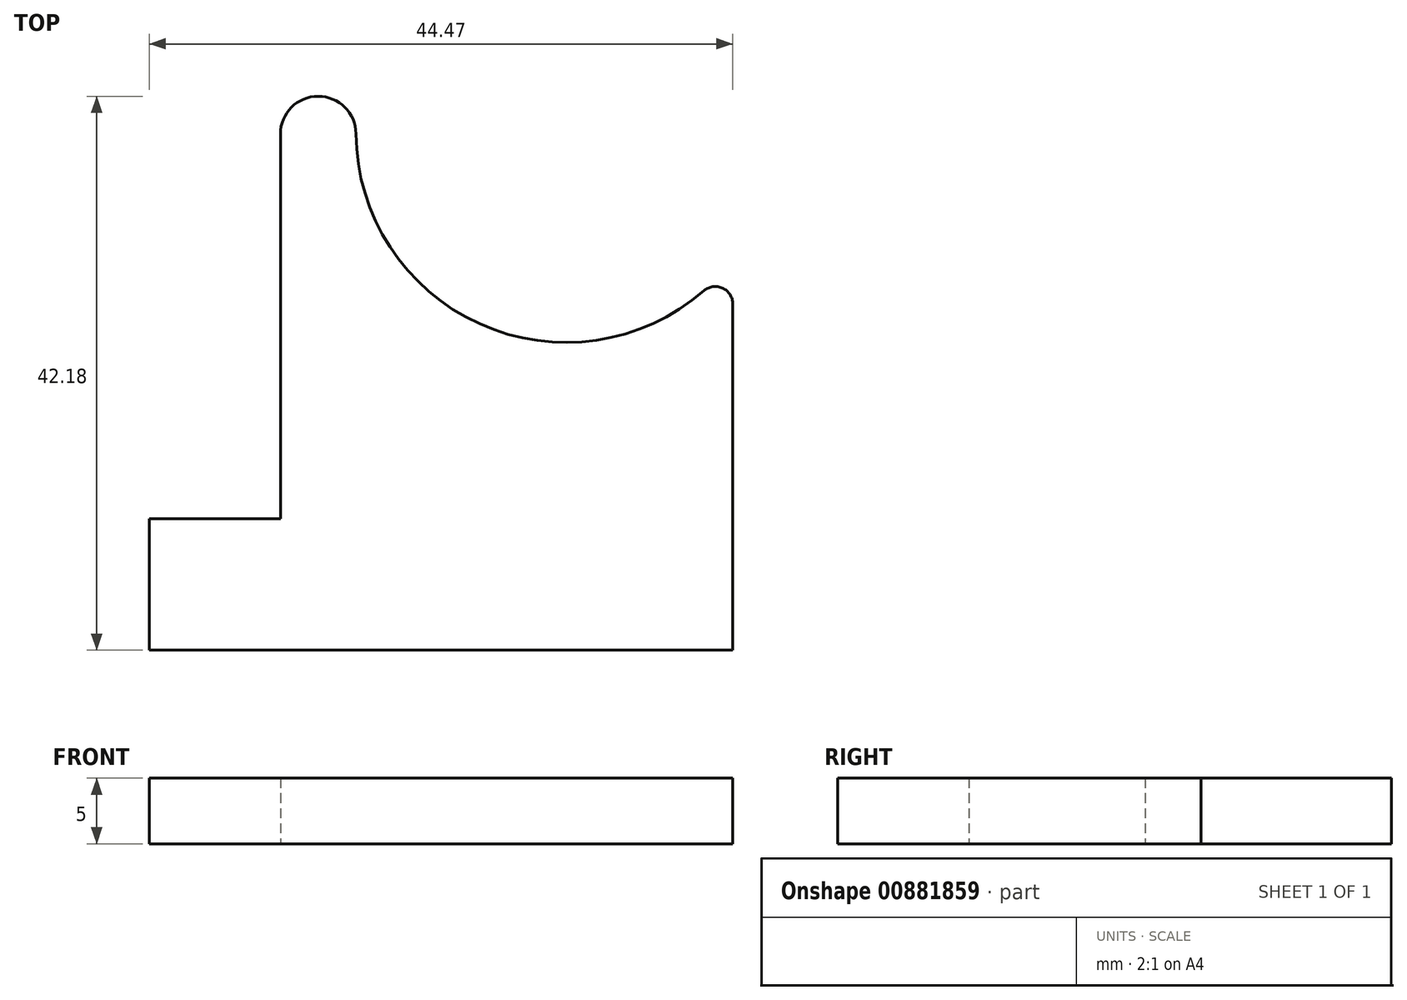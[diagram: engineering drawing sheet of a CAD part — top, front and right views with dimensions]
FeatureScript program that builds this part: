
annotation { "Feature Type Name" : "Feature", "Feature Type Description" : "" }
export const myFeature = defineFeature(function(context is Context, id is Id, definition is map)
    precondition{}
    {
        {
            var Q0;
            Q0=qCreatedBy(makeId("Top.planeOp"),FACE);
            var sketch = newSketch(context, id + "F0", { "sketchPlane" : qUnion([Q0])});
            skLineSegment(sketch, "E0.bottom", {"start": v(0, 0) * mm, "end": v(34.47, 0) * mm});
            skLineSegment(sketch, "E0.left", {"start": v(0, 0) * mm, "end": v(0, 29.3) * mm});
            skLineSegment(sketch, "E0.right", {"start": v(34.47, 0) * mm, "end": v(34.47, 16.35) * mm});
            skArc(sketch, "E1", {"start": v(5.76, 29.32) * mm, "mid": v(15.17, 14.85) * mm, "end": v(32.26, 17.36) * mm});
            skCircle(sketch, "E2", {"center": v(33.13, 16.35) * mm, "radius": 1.34 * mm});
            skCircle(sketch, "E3", {"center": v(2.88, 29.3) * mm, "radius": 2.88 * mm});
            skSolve(sketch);
        }
        {
            var Q0;
            Q0=qSketchRegion(id+"F0",true);
            extrude(context, id + "F1", {"entities" : qUnion([Q0]), "depth" : 5 * mm, "offsetDistance" : 25 * mm});
        }
        {
            var Q0;
            Q0=makeQuery(id+"F1.opExtrude","CAP_FACE",FACE,{"disambiguationData":[OSD([sQuery(id+"F0.wireOp",EDGE,"E0.bottom"),sQuery(id+"F0.wireOp",EDGE,"E0.left"),sQuery(id+"F0.wireOp",EDGE,"E0.right"),sQuery(id+"F0.wireOp",EDGE,"E1"),sQuery(id+"F0.wireOp",EDGE,"E2"),sQuery(id+"F0.wireOp",EDGE,"E3")])],"isStart":false});
            var sketch = newSketch(context, id + "F2", { "sketchPlane" : qUnion([Q0])});
            skLineSegment(sketch, "E4", {"start": v(34.47, 0) * mm, "end": v(34.47, -10) * mm});
            skLineSegment(sketch, "E5", {"start": v(34.47, -10) * mm, "end": v(0, -10) * mm});
            skLineSegment(sketch, "E6", {"start": v(0, -10) * mm, "end": v(0, 0) * mm});
            skLineSegment(sketch, "E7", {"start": v(0, 0) * mm, "end": v(-10, 0) * mm});
            skLineSegment(sketch, "E8", {"start": v(0, 25.49) * mm, "end": v(-110.38, 52.94) * mm});
            skLineSegment(sketch, "E9", {"start": v(0, -10) * mm, "end": v(-10, -10) * mm});
            skLineSegment(sketch, "E10", {"start": v(-10, -10) * mm, "end": v(-10, 0) * mm});
            skSolve(sketch);
        }
        {
            var Q0;
            {var subQ0=makeQuery(id+"F1.opExtrude","CAP_EDGE",EDGE,{"disambiguationData":[OSD([sQuery(id+"F0.wireOp",EDGE,"E0.bottom")])],"isStart":false});Q0=makeQuery(id+"F2.imprint","IMPRINT",FACE,{"disambiguationData":[TD([[makeQuery(id+"F2.imprint","IMPRINT",EDGE,{"derivedFrom":subQ0}),1.0]])]});}
            var Q1;
            Q1=makeQuery(id+"F2.imprint","IMPRINT",FACE,{"disambiguationData":[TD([[makeQuery(id+"F2.imprint","IMPRINT",EDGE,{"derivedFrom":sQuery(id+"F2.wireOp",EDGE,"E4")}),-1.0]])]});
            var Q2;
            {var subQ0=sQuery(id+"F2.wireOp",EDGE,"E7");Q2=makeQuery(id+"F2.imprint","IMPRINT",FACE,{"disambiguationData":[TD([[makeQuery(id+"F2.imprint","IMPRINT",EDGE,{"derivedFrom":subQ0}),-1.0]])]});}
            var Q3;
            Q3=makeQuery(id+"F2.imprint","IMPRINT",FACE,{"disambiguationData":[TD([[makeQuery(id+"F2.imprint","IMPRINT",EDGE,{"derivedFrom":sQuery(id+"F2.wireOp",EDGE,"E6")}),1.0]])]});
            extrude(context, id + "F3", {"entities" : qUnion([Q0, Q1, Q2, Q3]), "operationType" : NewBodyOperationType.ADD, "oppositeDirection" : true, "depth" : 5 * mm, "offsetDistance" : 25 * mm});
        }
    });
